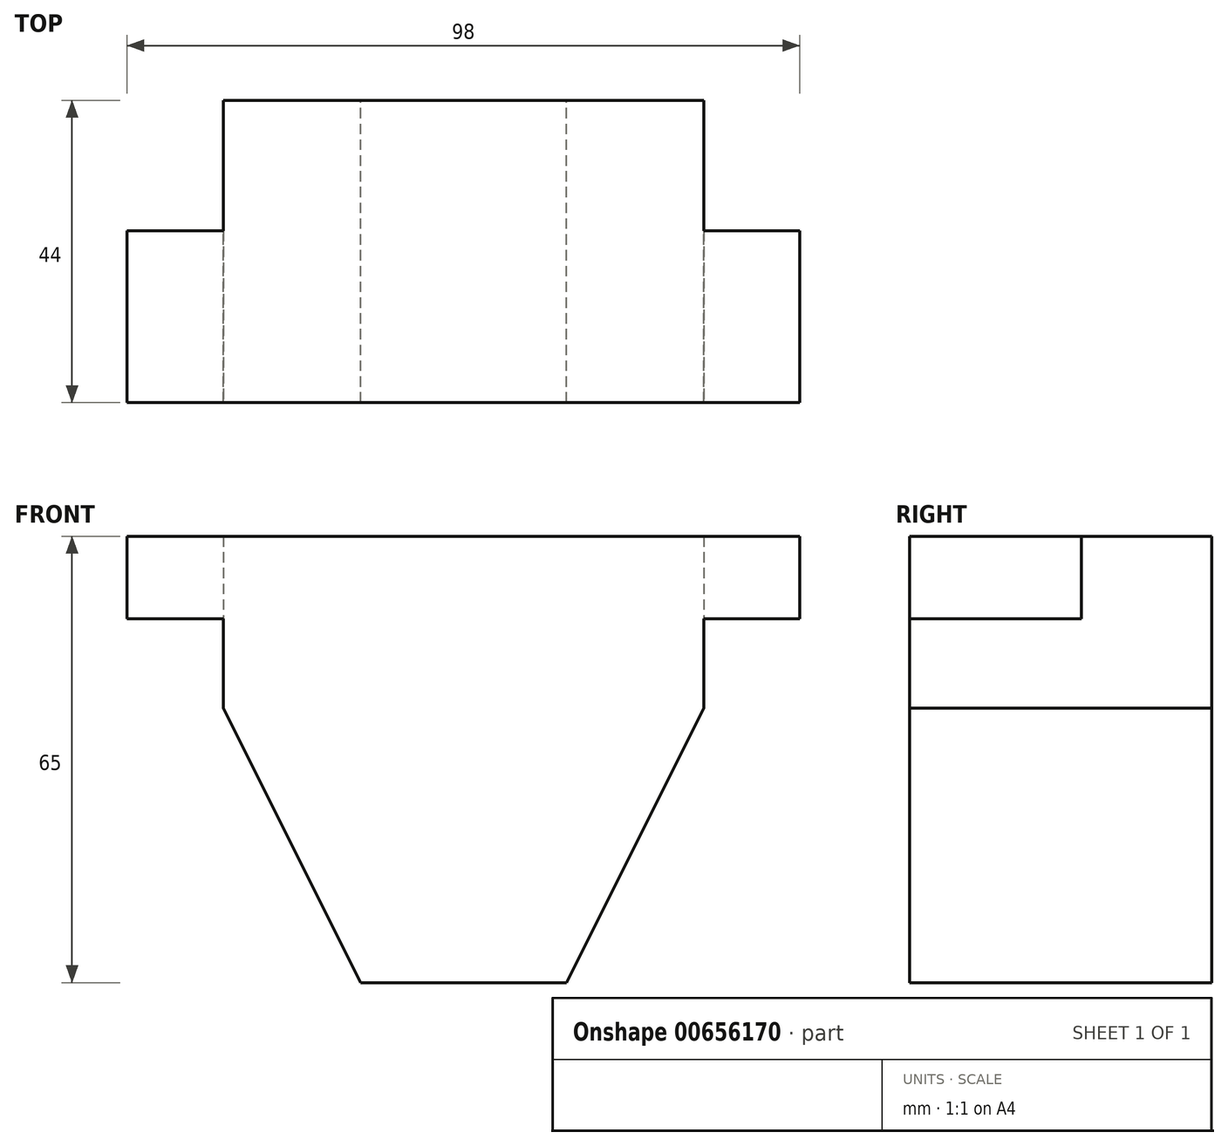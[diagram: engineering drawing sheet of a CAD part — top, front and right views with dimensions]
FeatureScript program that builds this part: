
annotation { "Feature Type Name" : "Feature", "Feature Type Description" : "" }
export const myFeature = defineFeature(function(context is Context, id is Id, definition is map)
    precondition{}
    {
        {
            var Q0;
            Q0=qCreatedBy(makeId("Front.planeOp"),FACE);
            var sketch = newSketch(context, id + "F0", { "sketchPlane" : qUnion([Q0])});
            skLineSegment(sketch, "E0.bottom", {"start": v(35, 32.5) * mm, "end": v(-35, 32.5) * mm});
            skLineSegment(sketch, "E0.top", {"start": v(15, -32.5) * mm, "end": v(-15, -32.5) * mm});
            skLineSegment(sketch, "E0.left", {"start": v(35, 32.5) * mm, "end": v(35, 7.5) * mm});
            skLineSegment(sketch, "E0.right", {"start": v(-35, 32.5) * mm, "end": v(-35, 7.5) * mm});
            skPoint(sketch, "E0.middle", {"position": v(0, 0) * mm});
            skPoint(sketch, "E1", {"position": v(-15, -32.5) * mm});
            skPoint(sketch, "E2", {"position": v(15, -32.5) * mm});
            skLineSegment(sketch, "E3", {"start": v(-35, 7.5) * mm, "end": v(-15, -32.5) * mm});
            skLineSegment(sketch, "E4", {"start": v(35, 7.5) * mm, "end": v(15, -32.5) * mm});
            skPoint(sketch, "E5.orphan", {"position": v(-35, -32.5) * mm});
            skPoint(sketch, "E6.orphan", {"position": v(35, -32.5) * mm});
            skPoint(sketch, "E7.oppositeSnap0", {"position": v(-35, 20) * mm});
            skLineSegment(sketch, "E7.left", {"start": v(-35, 32.5) * mm, "end": v(-35, 20) * mm});
            skLineSegment(sketch, "E8.bottom", {"start": v(-35, 32.5) * mm, "end": v(-49, 32.5) * mm});
            skLineSegment(sketch, "E8.top", {"start": v(-35, 20.5) * mm, "end": v(-49, 20.5) * mm});
            skLineSegment(sketch, "E8.left", {"start": v(-35, 32.5) * mm, "end": v(-35, 20.5) * mm});
            skLineSegment(sketch, "E8.right", {"start": v(-49, 32.5) * mm, "end": v(-49, 20.5) * mm});
            skLineSegment(sketch, "E9.bottom", {"start": v(35, 32.5) * mm, "end": v(35, 32.5) * mm});
            skLineSegment(sketch, "E9.top", {"start": v(35, 20.5) * mm, "end": v(35, 20.5) * mm});
            skLineSegment(sketch, "E9.left", {"start": v(35, 32.5) * mm, "end": v(35, 20.5) * mm});
            skLineSegment(sketch, "E9.right", {"start": v(35, 32.5) * mm, "end": v(35, 20.5) * mm});
            skLineSegment(sketch, "E10.bottom", {"start": v(35, 32.5) * mm, "end": v(49, 32.5) * mm});
            skLineSegment(sketch, "E10.top", {"start": v(35, 20.5) * mm, "end": v(49, 20.5) * mm});
            skLineSegment(sketch, "E10.right", {"start": v(49, 32.5) * mm, "end": v(49, 20.5) * mm});
            skSolve(sketch);
        }
        {
            var Q0;
            Q0=makeQuery(id+"F0.imprint","IMPRINT",FACE,{"disambiguationData":[TD([[makeQuery(id+"F0.imprint","IMPRINT",EDGE,{"derivedFrom":sQuery(id+"F0.wireOp",EDGE,"E0.bottom")}),1.0]])]});
            extrude(context, id + "F1", {"entities" : qUnion([Q0]), "depth" : 44 * mm, "offsetDistance" : 25 * mm});
        }
        {
            var Q0;
            Q0=makeQuery(id+"F1.opExtrude","CAP_FACE",FACE,{"disambiguationData":[OSD([sQuery(id+"F0.wireOp",EDGE,"E0.bottom"),sQuery(id+"F0.wireOp",EDGE,"E0.top"),sQuery(id+"F0.wireOp",EDGE,"E0.left"),sQuery(id+"F0.wireOp",EDGE,"E0.right"),sQuery(id+"F0.wireOp",EDGE,"E3"),sQuery(id+"F0.wireOp",EDGE,"E4"),sQuery(id+"F0.wireOp",EDGE,"E7.left"),sQuery(id+"F0.wireOp",EDGE,"E8.bottom"),sQuery(id+"F0.wireOp",EDGE,"E8.top"),sQuery(id+"F0.wireOp",EDGE,"E8.right"),sQuery(id+"F0.wireOp",EDGE,"E10.bottom"),sQuery(id+"F0.wireOp",EDGE,"E10.top"),sQuery(id+"F0.wireOp",EDGE,"E10.right")])],"isStart":false});
            var sketch = newSketch(context, id + "F2", { "sketchPlane" : qUnion([Q0])});
            skLineSegment(sketch, "E11", {"start": v(-35, 32.5) * mm, "end": v(-35, 32.5) * mm});
            skLineSegment(sketch, "E12", {"start": v(35, 7.5) * mm, "end": v(35, 32.5) * mm});
            skLineSegment(sketch, "E13.bottom", {"start": v(-35, 32.5) * mm, "end": v(-49, 32.5) * mm});
            skLineSegment(sketch, "E13.top", {"start": v(-35, 20.5) * mm, "end": v(-49, 20.5) * mm});
            skLineSegment(sketch, "E13.left", {"start": v(-35, 32.5) * mm, "end": v(-35, 20.5) * mm});
            skLineSegment(sketch, "E13.right", {"start": v(-49, 32.5) * mm, "end": v(-49, 20.5) * mm});
            skLineSegment(sketch, "E14.bottom", {"start": v(35, 32.5) * mm, "end": v(49, 32.5) * mm});
            skLineSegment(sketch, "E14.top", {"start": v(35, 20.5) * mm, "end": v(49, 20.5) * mm});
            skLineSegment(sketch, "E14.left", {"start": v(35, 32.5) * mm, "end": v(35, 20.5) * mm});
            skLineSegment(sketch, "E14.right", {"start": v(49, 32.5) * mm, "end": v(49, 20.5) * mm});
            skSolve(sketch);
        }
        {
            var Q0;
            Q0=makeQuery(id+"F2.imprint","IMPRINT",FACE,{"disambiguationData":[TD([[makeQuery(id+"F2.imprint","IMPRINT",EDGE,{"derivedFrom":sQuery(id+"F2.wireOp",EDGE,"E13.bottom")}),1.0]])]});
            var Q1;
            Q1=makeQuery(id+"F2.imprint","IMPRINT",FACE,{"disambiguationData":[TD([[makeQuery(id+"F2.imprint","IMPRINT",EDGE,{"derivedFrom":sQuery(id+"F2.wireOp",EDGE,"E14.bottom")}),-1.0]])]});
            extrude(context, id + "F3", {"entities" : qUnion([Q0, Q1]), "operationType" : NewBodyOperationType.ADD, "oppositeDirection" : true, "depth" : 25 * mm, "offsetDistance" : 25 * mm});
        }
    });
